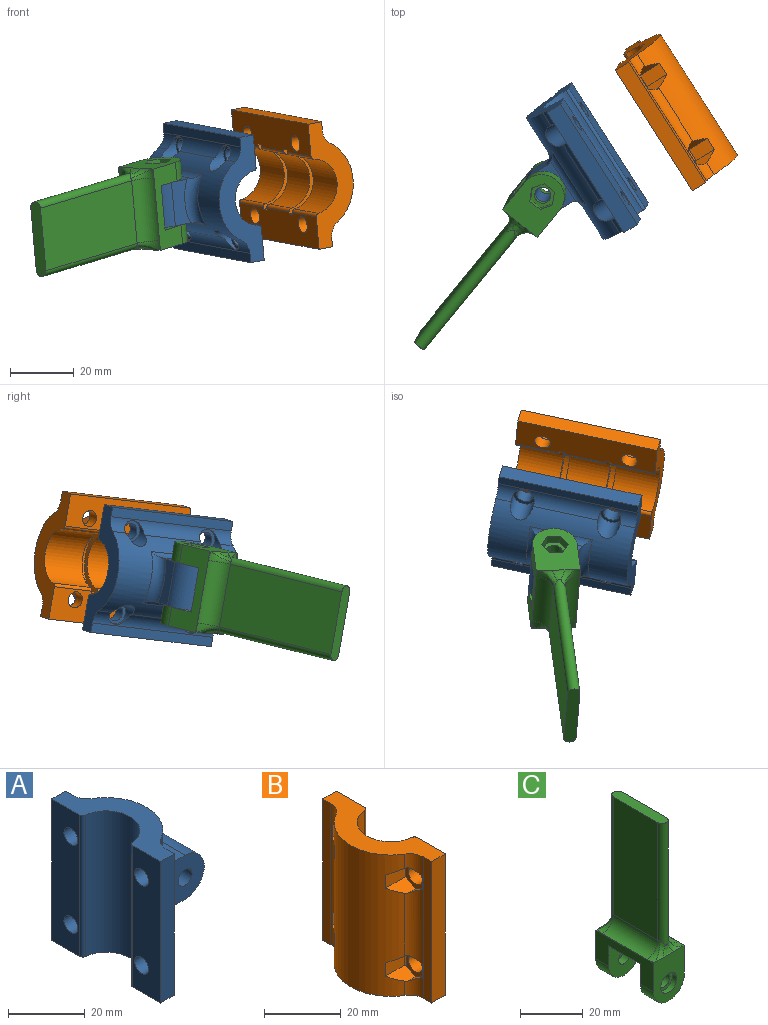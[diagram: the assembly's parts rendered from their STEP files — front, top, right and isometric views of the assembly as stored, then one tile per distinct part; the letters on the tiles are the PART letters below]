
ASSEMBLY  parts=3 mates=2
PART A: 36 faces, bbox 29x40x45 mm
  f0: cylinder r=5mm len=45mm, axis (0,0,-1), area 176.2mm2, adj f1,f3,f5,f6,f12,f13
  f1: cylinder r=14.71mm len=45mm, axis (0,0,-1), area 907.3mm2, adj f0,f2,f5,f6,f12,f13,f14,f15
  f2: cylinder r=5mm len=45mm, axis (0,0,-1), area 176.2mm2, adj f1,f4,f5,f6,f14,f15
  f3: plane 45x3.01mm, normal (1,0,0), area 135.4mm2, adj f0,f5,f6,f8
  f4: plane 45x3.01mm, normal (1,0,0), area 135.4mm2, adj f2,f5,f6,f9
  f5: plane 40x14.72mm, normal (0,0,-1), area 279.3mm2, adj f0,f1,f2,f3,f4,f7,f8,f9
  f6: plane 40x14.72mm, normal (0,0,1), area 279.3mm2, adj f0,f1,f2,f3,f4,f7,f8,f9
  f7: cylinder r=8.71mm len=45mm, axis (0,0,-1), area 1151.2mm2, adj f5,f6,f34,f35
  f8: plane 45x5mm, normal (0,-1,0), area 225mm2, adj f3,f5,f6,f11
  f9: plane 45x5mm, normal (0,1,0), area 225mm2, adj f4,f5,f6,f10
  f10: plane 45x10.34mm, normal (-1,0,0), area 424.3mm2, adj f5,f6,f9,f20,f22,f35
  f11: plane 45x10.34mm, normal (-1,0,0), area 424.3mm2, adj f5,f6,f8,f16,f18,f34
  f12: cylinder r=3.6mm len=7.32mm, axis (-1,0,0), area 83.8mm2, adj f0,f1,f17
  f13: cylinder r=3.6mm len=7.32mm, axis (-1,0,0), area 83.8mm2, adj f0,f1,f19
  f14: cylinder r=3.6mm len=7.32mm, axis (-1,0,0), area 83.8mm2, adj f1,f2,f21
  f15: cylinder r=3.6mm len=7.32mm, axis (-1,0,0), area 83.8mm2, adj f1,f2,f23
  f16: cylinder r=2.55mm len=5.1mm, axis (-1,0,0), area 64.1mm2, adj f11,f17
  f17: plane 7.2x7.2mm, normal (1,0,0), area 20.3mm2, adj f12,f16
  f18: cylinder r=2.55mm len=5.1mm, axis (-1,0,0), area 64.1mm2, adj f11,f19
  f19: plane 7.2x7.2mm, normal (1,0,0), area 20.3mm2, adj f13,f18
  f20: cylinder r=2.55mm len=5.1mm, axis (-1,0,0), area 64.1mm2, adj f10,f21
  f21: plane 7.2x7.2mm, normal (1,0,0), area 20.3mm2, adj f14,f20
  f22: cylinder r=2.55mm len=5.1mm, axis (-1,0,0), area 64.1mm2, adj f10,f23
  f23: plane 7.2x7.2mm, normal (1,0,0), area 20.3mm2, adj f15,f22
  f24: plane 14.82x14.39mm, normal (0,1,0), area 160.3mm2, adj f26,f27,f28,f29,f31,f32,f33
  f25: plane 14.82x14.39mm, normal (0,-1,0), area 160.3mm2, adj f26,f27,f28,f30,f31,f32,f33
  f26: plane 14x5.73mm, normal (0,0,-1), area 66.6mm2, adj f24,f25,f31,f32
  f27: plane 14x5.73mm, normal (0,0,1), area 66.6mm2, adj f24,f25,f28,f32
  f28: torus R=17.71mm, axis (0,0,-1), area 71.7mm2, adj f1,f24,f25,f27,f29,f30
  f29: cylinder r=3mm len=20mm, axis (0,0,-1), area 49.9mm2, adj f1,f24,f28,f31
  f30: cylinder r=3mm len=20mm, axis (0,0,-1), area 49.9mm2, adj f1,f25,f28,f31
  f31: torus R=17.71mm, axis (0,0,-1), area 71.7mm2, adj f1,f24,f25,f26,f29,f30
  f32: cylinder r=7mm len=14mm, axis (0,-1,0), area 307.9mm2, adj f24,f25,f26,f27
  f33: cylinder r=2.55mm len=14mm, axis (0,-1,0), area 224.3mm2, adj f24,f25
  f34: cylinder r=1mm len=45mm, axis (0,0,-1), area 66mm2, adj f5,f6,f7,f11
  f35: cylinder r=1mm len=45mm, axis (0,0,-1), area 66mm2, adj f5,f6,f7,f10
PART B: 60 faces, bbox 14.7x40x45 mm
  f0: plane 45x10.34mm, normal (1,0,0), area 421.3mm2, adj f2,f7,f10,f41,f42,f44,f45,f47
  f1: plane 45x10.34mm, normal (1,0,0), area 421.3mm2, adj f2,f8,f10,f38,f40,f44,f45,f47
  f2: plane 40x14.72mm, normal (0,0,-1), area 279.3mm2, adj f0,f1,f7,f8,f11,f12,f13,f14
  f3: plane 6.84x4.16mm, normal (0,-1,0), area 28.4mm2, adj f12,f24,f25,f51
  f4: plane 6.84x4.16mm, normal (0,1,0), area 28.4mm2, adj f12,f27,f31,f50
  f5: plane 8.31x6.98mm, normal (-1,0,0), area 23.5mm2, adj f22,f23,f24,f25,f26,f40,f51
  f6: plane 8.31x6.98mm, normal (-1,0,0), area 23.5mm2, adj f27,f28,f29,f30,f31,f41,f50
  f7: plane 45x5mm, normal (0,1,0), area 225mm2, adj f0,f2,f10,f11
  f8: plane 45x5mm, normal (0,-1,0), area 225mm2, adj f1,f2,f10,f13
  f9: cylinder r=8.71mm len=17.34mm, axis (0,0,-1), area 358.1mm2, adj f10,f45,f58,f59
  f10: plane 40x14.72mm, normal (0,0,1), area 279.3mm2, adj f0,f1,f7,f8,f9,f11,f12,f13
  f11: plane 45x3.01mm, normal (-1,0,0), area 135.4mm2, adj f2,f7,f10,f15
  f12: cylinder r=14.71mm len=45mm, axis (0,0,-1), area 1250mm2, adj f2,f3,f4,f10,f14,f15,f18,f19
  f13: plane 45x3.01mm, normal (-1,0,0), area 135.4mm2, adj f2,f8,f10,f14
  f14: cylinder r=5mm len=45mm, axis (0,0,-1), area 170.3mm2, adj f2,f10,f12,f13,f16,f17,f18,f20
  f15: cylinder r=5mm len=45mm, axis (0,0,-1), area 170.3mm2, adj f2,f10,f11,f12,f27,f28,f29,f30
  f16: plane 4.16x1.02mm, normal (0,1,0), area 4.2mm2, adj f14,f17,f21,f39
  f17: plane 3.6x2.99mm, normal (0,0.5,0.87), area 6.9mm2, adj f14,f16,f18,f39
  f18: plane 7.33x3.61mm, normal (0,-0.5,0.87), area 22.5mm2, adj f12,f14,f17,f19,f39
  f19: plane 7.32x4.16mm, normal (0,-1,0), area 30.4mm2, adj f12,f18,f20,f39
  f20: plane 7.33x3.61mm, normal (0,-0.5,-0.87), area 22.5mm2, adj f12,f14,f19,f21,f39
  f21: plane 3.6x2.99mm, normal (0,0.5,-0.87), area 6.9mm2, adj f14,f16,f20,f39
  f22: plane 4.16x1.02mm, normal (0,1,0), area 4.2mm2, adj f5,f14,f23,f26
  f23: plane 3.6x2.99mm, normal (0,0.5,0.87), area 6.9mm2, adj f5,f14,f22,f24
  f24: plane 7.33x3.61mm, normal (0,-0.5,0.87), area 22.4mm2, adj f3,f5,f12,f14,f23,f51
  f25: plane 7.33x3.61mm, normal (0,-0.5,-0.87), area 22.4mm2, adj f3,f5,f12,f14,f26,f51
  f26: plane 3.6x2.99mm, normal (0,0.5,-0.87), area 6.9mm2, adj f5,f14,f22,f25
  f27: plane 7.33x3.61mm, normal (0,0.5,0.87), area 22.4mm2, adj f4,f6,f12,f15,f28,f50
  f28: plane 3.6x2.99mm, normal (0,-0.5,0.87), area 6.9mm2, adj f6,f15,f27,f29
  f29: plane 4.16x1.02mm, normal (0,-1,0), area 4.2mm2, adj f6,f15,f28,f30
  f30: plane 3.6x2.99mm, normal (0,-0.5,-0.87), area 6.9mm2, adj f6,f15,f29,f31
  f31: plane 7.33x3.61mm, normal (0,0.5,-0.87), area 22.4mm2, adj f4,f6,f12,f15,f30,f50
  f32: plane 7.32x4.16mm, normal (0,1,0), area 30.4mm2, adj f12,f33,f37,f43
  f33: plane 7.33x3.61mm, normal (0,0.5,0.87), area 22.5mm2, adj f12,f15,f32,f34,f43
  f34: plane 3.6x2.99mm, normal (0,-0.5,0.87), area 6.9mm2, adj f15,f33,f35,f43
  f35: plane 4.16x1.02mm, normal (0,-1,0), area 4.2mm2, adj f15,f34,f36,f43
  f36: plane 3.6x2.99mm, normal (0,-0.5,-0.87), area 6.9mm2, adj f15,f35,f37,f43
  f37: plane 7.33x3.61mm, normal (0,0.5,-0.87), area 22.5mm2, adj f12,f15,f32,f36,f43
  f38: cylinder r=2.55mm len=5.1mm, axis (1,0,0), area 64.1mm2, adj f1,f39
  f39: plane 8.31x7.2mm, normal (-1,0,0), area 24.5mm2, adj f16,f17,f18,f19,f20,f21,f38
  f40: cylinder r=2.55mm len=5.1mm, axis (1,0,0), area 64.1mm2, adj f1,f5
  f41: cylinder r=2.55mm len=5.1mm, axis (1,0,0), area 64.1mm2, adj f0,f6
  f42: cylinder r=2.55mm len=5.1mm, axis (1,0,0), area 64.1mm2, adj f0,f43
  f43: plane 8.31x7.2mm, normal (-1,0,0), area 24.5mm2, adj f32,f33,f34,f35,f36,f37,f42
  f44: cylinder r=10.42mm len=20.83mm, axis (0,0,-1), area 65.4mm2, adj f0,f1,f45,f47
  f45: plane 20.83x10.42mm, normal (0,0,-1), area 50.7mm2, adj f0,f1,f9,f44,f58,f59
  f46: cylinder r=8.71mm len=17.34mm, axis (0,0,-1), area 332.6mm2, adj f47,f49,f56,f57
  f47: plane 20.83x10.42mm, normal (0,0,1), area 50.7mm2, adj f0,f1,f44,f46,f56,f57
  f48: cylinder r=10.42mm len=20.83mm, axis (0,0,-1), area 65.4mm2, adj f0,f1,f49,f53
  f49: plane 20.83x10.42mm, normal (0,0,-1), area 50.7mm2, adj f0,f1,f46,f48,f56,f57
  f50: cylinder r=10.42mm len=4.41mm, axis (0,0,-1), area 2.3mm2, adj f4,f6,f27,f31
  f51: cylinder r=10.42mm len=4.41mm, axis (0,0,-1), area 2.3mm2, adj f3,f5,f24,f25
  f52: cylinder r=8.71mm len=17.34mm, axis (0,0,-1), area 358.1mm2, adj f2,f53,f54,f55
  f53: plane 20.83x10.42mm, normal (0,0,1), area 50.7mm2, adj f0,f1,f48,f52,f54,f55
  f54: cylinder r=1mm len=14mm, axis (0,0,-1), area 20.5mm2, adj f0,f2,f52,f53
  f55: cylinder r=1mm len=14mm, axis (0,0,-1), area 20.5mm2, adj f1,f2,f52,f53
  f56: cylinder r=1mm len=13mm, axis (0,0,-1), area 19.1mm2, adj f0,f46,f47,f49
  f57: cylinder r=1mm len=13mm, axis (0,0,-1), area 19.1mm2, adj f1,f46,f47,f49
  f58: cylinder r=1mm len=14mm, axis (0,0,-1), area 20.5mm2, adj f1,f9,f10,f45
  f59: cylinder r=1mm len=14mm, axis (0,0,-1), area 20.5mm2, adj f0,f9,f10,f45
PART C: 39 faces, bbox 22.8x29.9x69.3 mm
  f0: bspline ~5.96x3.87mm, area 9.3mm2, adj f1,f5,f11,f19
  f1: bspline ~5.68x5mm, area 10.8mm2, adj f0,f5,f11,f21
  f2: bspline ~5.96x3.87mm, area 9.3mm2, adj f3,f7,f13,f18
  f3: bspline ~5.68x5mm, area 10.8mm2, adj f2,f7,f13,f16
  f4: plane 26x0.73mm, normal (0,0,1), area 2.6mm2, adj f5,f7,f8,f20,f21,f22
  f5: plane 18.26x14.06mm, normal (0,1,0), area 188.9mm2, adj f0,f1,f4,f6,f8,f9,f19,f26
  f6: plane 26x11.2mm, normal (-1,0,0), area 177.6mm2, adj f5,f7,f9,f23,f24,f25,f26,f38
  f7: plane 18.26x14.06mm, normal (0,-1,0), area 191.9mm2, adj f2,f3,f4,f6,f8,f9,f18,f25
  f8: plane 26x11.2mm, normal (1,0,0), area 177.6mm2, adj f4,f5,f7,f23,f24,f25,f26,f38
  f9: plane 26x0.73mm, normal (0,0,1), area 2.6mm2, adj f5,f6,f7,f15,f16,f17
  f10: plane 46x20mm, normal (1,0,0), area 920mm2, adj f11,f13,f14,f22
  f11: cylinder r=1.95mm len=47.56mm, axis (0,0,-1), area 286.1mm2, adj f0,f1,f10,f12,f14,f17,f19,f21
  f12: plane 46x20mm, normal (-1,0,0), area 920mm2, adj f11,f13,f14,f15
  f13: cylinder r=1.95mm len=47.56mm, axis (0,0,-1), area 286.1mm2, adj f2,f3,f10,f12,f14,f16,f18,f20
  f14: plane 23.9x3.9mm, normal (0,0,1), area 89.9mm2, adj f10,f11,f12,f13
  f15: cylinder r=5mm len=20mm, axis (0,1,0), area 157.1mm2, adj f9,f12,f16,f17
  f16: torus R=6.95mm, axis (0,0,1), area 13.2mm2, adj f3,f9,f13,f15
  f17: torus R=6.95mm, axis (0,0,1), area 13.2mm2, adj f9,f11,f15,f19
  f18: bspline ~5.68x5mm, area 10.8mm2, adj f2,f7,f13,f20
  f19: bspline ~5.68x5mm, area 10.8mm2, adj f0,f5,f11,f17
  f20: torus R=6.95mm, axis (0,0,1), area 13.2mm2, adj f4,f13,f18,f22
  f21: torus R=6.95mm, axis (0,0,1), area 13.2mm2, adj f1,f4,f11,f22
  f22: cylinder r=5mm len=20mm, axis (0,-1,0), area 157.1mm2, adj f4,f10,f20,f21
  f23: plane 15x14mm, normal (0,1,0), area 168.5mm2, adj f6,f8,f25,f37,f38
  f24: plane 15x14mm, normal (0,-1,0), area 168.5mm2, adj f6,f8,f26,f36,f38
  f25: cylinder r=7mm len=14mm, axis (0,1,0), area 129.7mm2, adj f6,f7,f8,f23
  f26: cylinder r=7mm len=14mm, axis (0,-1,0), area 129.7mm2, adj f5,f6,f8,f24
  f27: cylinder r=3.65mm len=7.3mm, axis (0,-1,0), area 45.9mm2, adj f7,f28
  f28: plane 7.3x7.3mm, normal (0,-1,0), area 21.4mm2, adj f27,f37
  f29: plane 3.6x3mm, normal (-0.87,0,0.5), area 12.5mm2, adj f5,f30,f34,f35
  f30: plane 4.16x3mm, normal (0,0,1), area 12.5mm2, adj f5,f29,f31,f35
  f31: plane 3.6x3mm, normal (0.87,0,0.5), area 12.5mm2, adj f5,f30,f32,f35
  f32: plane 3.6x3mm, normal (0.87,0,-0.5), area 12.5mm2, adj f5,f31,f33,f35
  f33: plane 4.16x3mm, normal (0,0,-1), area 12.5mm2, adj f5,f32,f34,f35
  f34: plane 3.6x3mm, normal (-0.87,0,-0.5), area 12.5mm2, adj f5,f29,f33,f35
  f35: plane 8.31x7.2mm, normal (0,1,0), area 24.5mm2, adj f29,f30,f31,f32,f33,f34,f36
  f36: cylinder r=2.55mm len=5.1mm, axis (0,-1,0), area 46.5mm2, adj f24,f35
  f37: cylinder r=2.55mm len=5.1mm, axis (0,-1,0), area 62.5mm2, adj f23,f28
  f38: plane 14.2x14mm, normal (0,0,-1), area 198.8mm2, adj f6,f8,f23,f24
PLACE A rot(axis=(0.24,-0.63,-0.73),163deg) t=(30,53.71,-34.67)mm
PLACE B rot(axis=(0.24,-0.63,-0.73),163deg) t=(47.24,64.3,-31.3)mm
PLACE C rot(axis=(0.91,-0.3,-0.28),106.9deg) t=(-4.93,55.84,-37.47)mm
MATE slider A.f13 <-> B.f40  axis (0.84,0.52,0.16) through (26.57,63.07,-46.58)mm
MATE revolute A.f33 <-> C.f36  axis (-0.09,-0.17,0.98) through (-1.13,60.02,-29.17)mm
